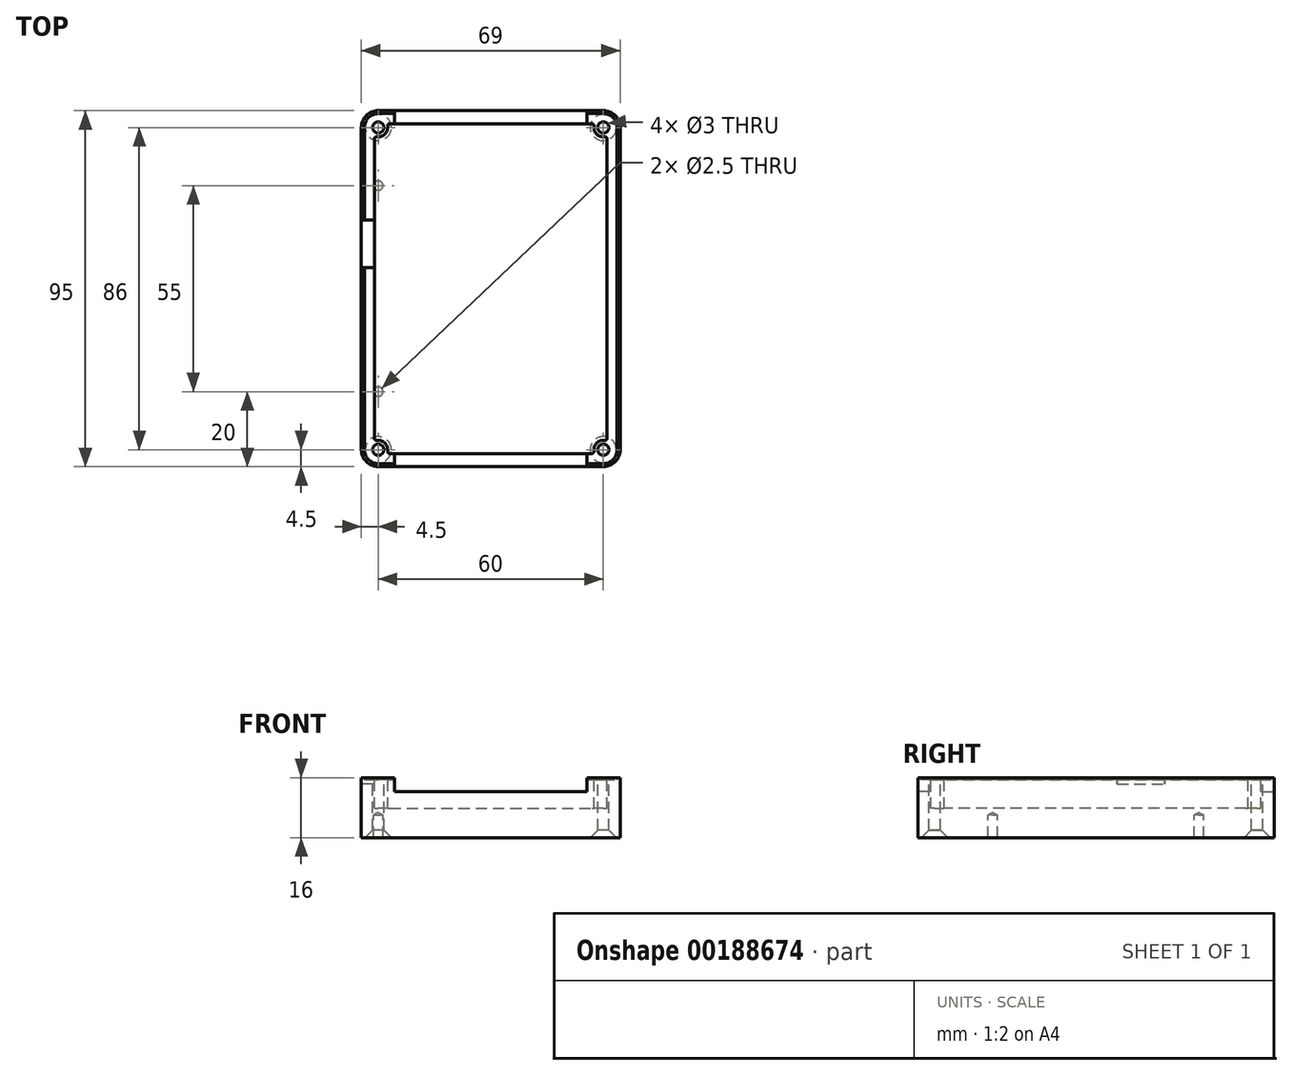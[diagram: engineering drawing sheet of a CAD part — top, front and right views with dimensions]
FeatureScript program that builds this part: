
annotation { "Feature Type Name" : "Feature", "Feature Type Description" : "" }
export const myFeature = defineFeature(function(context is Context, id is Id, definition is map)
    precondition{}
    {
        {
            var Q0;
            Q0=qCreatedBy(makeId("Top.planeOp"),FACE);
            var sketch = newSketch(context, id + "F0", { "sketchPlane" : qUnion([Q0])});
            skLineSegment(sketch, "E0.bottom", {"start": v(34.5, 47.5) * mm, "end": v(-34.5, 47.5) * mm});
            skLineSegment(sketch, "E0.top", {"start": v(34.5, -47.5) * mm, "end": v(-34.5, -47.5) * mm});
            skLineSegment(sketch, "E0.left", {"start": v(34.5, 47.5) * mm, "end": v(34.5, -47.5) * mm});
            skLineSegment(sketch, "E0.right", {"start": v(-34.5, 47.5) * mm, "end": v(-34.5, -47.5) * mm});
            skPoint(sketch, "E0.middle", {"position": v(0, 0) * mm});
            skSolve(sketch);
        }
        {
            var Q0;
            Q0=makeQuery(id+"F0.imprint","IMPRINT",FACE,{"disambiguationData":[TD([[makeQuery(id+"F0.imprint","IMPRINT",EDGE,{"derivedFrom":sQuery(id+"F0.wireOp",EDGE,"E0.bottom")}),1.0]])]});
            extrude(context, id + "F1", {"entities" : qUnion([Q0]), "flatOperationType" : FlatOperationType.REMOVE, "offsetDistance" : 25 * mm, "depth" : 15.5 * mm, "domain" : OperationDomain.MODEL});
        }
        {
            var Q0;
            Q0=makeQuery(id+"F1.opExtrude","SWEPT_EDGE",EDGE,{"disambiguationData":[OSD([sQuery(id+"F0.wireOp",EDGE,"E0.bottom"),sQuery(id+"F0.wireOp",EDGE,"E0.right")])]});
            var Q1;
            Q1=makeQuery(id+"F1.opExtrude","SWEPT_EDGE",EDGE,{"disambiguationData":[OSD([sQuery(id+"F0.wireOp",EDGE,"E0.top"),sQuery(id+"F0.wireOp",EDGE,"E0.right")])]});
            var Q2;
            Q2=makeQuery(id+"F1.opExtrude","SWEPT_EDGE",EDGE,{"disambiguationData":[OSD([sQuery(id+"F0.wireOp",EDGE,"E0.top"),sQuery(id+"F0.wireOp",EDGE,"E0.left")])]});
            var Q3;
            Q3=makeQuery(id+"F1.opExtrude","SWEPT_EDGE",EDGE,{"disambiguationData":[OSD([sQuery(id+"F0.wireOp",EDGE,"E0.bottom"),sQuery(id+"F0.wireOp",EDGE,"E0.left")])]});
            fillet(context, id + "F2", {"entities" : qUnion([Q0, Q1, Q2, Q3]), "radius" : 4.5 * mm, "tangentPropagation" : true, "allowEdgeOverflow" : false});
        }
        {
            var Q0;
            Q0=makeQuery(id+"F1.opExtrude","CAP_FACE",FACE,{"disambiguationData":[OSD([sQuery(id+"F0.wireOp",EDGE,"E0.bottom"),sQuery(id+"F0.wireOp",EDGE,"E0.top"),sQuery(id+"F0.wireOp",EDGE,"E0.left"),sQuery(id+"F0.wireOp",EDGE,"E0.right")])],"isStart":false});
            var sketch = newSketch(context, id + "F3", { "sketchPlane" : qUnion([Q0])});
            skArc(sketch, "E1", {"start": v(-30, 40.5) * mm, "mid": v(-28.23, 41.23) * mm, "end": v(-27.5, 43) * mm});
            skArc(sketch, "E2", {"start": v(27.5, 43) * mm, "mid": v(28.23, 41.23) * mm, "end": v(30, 40.5) * mm});
            skArc(sketch, "E3", {"start": v(30, -40.5) * mm, "mid": v(28.23, -41.23) * mm, "end": v(27.5, -43) * mm});
            skArc(sketch, "E4", {"start": v(-27.5, -43) * mm, "mid": v(-28.23, -41.23) * mm, "end": v(-30, -40.5) * mm});
            skLineSegment(sketch, "E5", {"start": v(-30, 40.5) * mm, "end": v(-31, 40.5) * mm});
            skLineSegment(sketch, "E6", {"start": v(-31, 40.5) * mm, "end": v(-31, -40.5) * mm});
            skLineSegment(sketch, "E7", {"start": v(-31, -40.5) * mm, "end": v(-30, -40.5) * mm});
            skLineSegment(sketch, "E8", {"start": v(-27.5, -43) * mm, "end": v(-27.5, -44) * mm});
            skLineSegment(sketch, "E9", {"start": v(-27.5, -44) * mm, "end": v(27.5, -44) * mm});
            skLineSegment(sketch, "E10", {"start": v(27.5, -44) * mm, "end": v(27.5, -43) * mm});
            skLineSegment(sketch, "E11", {"start": v(30, -40.5) * mm, "end": v(31, -40.5) * mm});
            skLineSegment(sketch, "E12", {"start": v(31, -40.5) * mm, "end": v(31, 40.5) * mm});
            skLineSegment(sketch, "E13", {"start": v(31, 40.5) * mm, "end": v(30, 40.5) * mm});
            skLineSegment(sketch, "E14", {"start": v(27.5, 43) * mm, "end": v(27.5, 44) * mm});
            skLineSegment(sketch, "E15", {"start": v(27.5, 44) * mm, "end": v(-27.5, 44) * mm});
            skLineSegment(sketch, "E16", {"start": v(-27.5, 44) * mm, "end": v(-27.5, 43) * mm});
            skPoint(sketch, "E17.0", {"position": v(33.18, 46.18) * mm});
            skLineSegment(sketch, "E18.bottom", {"start": v(31, 44) * mm, "end": v(-31, 44) * mm, "construction": true});
            skLineSegment(sketch, "E18.top", {"start": v(31, -44) * mm, "end": v(-31, -44) * mm, "construction": true});
            skLineSegment(sketch, "E18.left", {"start": v(31, 44) * mm, "end": v(31, -44) * mm, "construction": true});
            skLineSegment(sketch, "E18.right", {"start": v(-31, 44) * mm, "end": v(-31, -44) * mm, "construction": true});
            skPoint(sketch, "E18.middle", {"position": v(0, 0) * mm});
            skSolve(sketch);
        }
        {
            var Q0;
            Q0=makeQuery(id+"F3.imprint","IMPRINT",FACE,{"disambiguationData":[TD([[makeQuery(id+"F3.imprint","IMPRINT",EDGE,{"derivedFrom":sQuery(id+"F3.wireOp",EDGE,"E1")}),-1.0]])]});
            extrude(context, id + "F4", {"entities" : qUnion([Q0]), "operationType" : NewBodyOperationType.REMOVE, "flatOperationType" : FlatOperationType.REMOVE, "oppositeDirection" : true, "offsetDistance" : 25 * mm, "depth" : (15.5 - 7.8) * mm, "domain" : OperationDomain.MODEL});
        }
        {
            var Q0;
            Q0=makeQuery(id+"F3.imprint","IMPRINT",FACE,{"disambiguationData":[TD([[makeQuery(id+"F3.imprint","IMPRINT",EDGE,{"derivedFrom":sQuery(id+"F3.wireOp",EDGE,"E1")}),1.0]])]});
            var sketch = newSketch(context, id + "F5", { "sketchPlane" : qUnion([Q0])});
            skLineSegment(sketch, "E19.0", {"start": v(-34.5, 43) * mm, "end": v(-34.5, -43) * mm});
            skArc(sketch, "E19.1", {"start": v(-30, 47.5) * mm, "mid": v(-33.18, 46.18) * mm, "end": v(-34.5, 43) * mm});
            skLineSegment(sketch, "E19.2", {"start": v(30, 47.5) * mm, "end": v(-30, 47.5) * mm});
            skLineSegment(sketch, "E19.3", {"start": v(34.5, 43) * mm, "end": v(34.5, -43) * mm});
            skArc(sketch, "E19.4", {"start": v(34.5, 43) * mm, "mid": v(33.18, 46.18) * mm, "end": v(30, 47.5) * mm});
            skArc(sketch, "E19.5", {"start": v(30, -47.5) * mm, "mid": v(33.18, -46.18) * mm, "end": v(34.5, -43) * mm});
            skLineSegment(sketch, "E19.6", {"start": v(30, -47.5) * mm, "end": v(-30, -47.5) * mm});
            skArc(sketch, "E19.7", {"start": v(-34.5, -43) * mm, "mid": v(-33.18, -46.18) * mm, "end": v(-30, -47.5) * mm});
            skLineSegment(sketch, "E20.0", {"start": v(30, 46.7) * mm, "end": v(-30, 46.7) * mm});
            skArc(sketch, "E20.1", {"start": v(33.7, 43) * mm, "mid": v(32.62, 45.62) * mm, "end": v(30, 46.7) * mm});
            skArc(sketch, "E20.2", {"start": v(-30, 46.7) * mm, "mid": v(-32.62, 45.62) * mm, "end": v(-33.7, 43) * mm});
            skLineSegment(sketch, "E20.3", {"start": v(33.7, 43) * mm, "end": v(33.7, -43) * mm});
            skLineSegment(sketch, "E20.4", {"start": v(-33.7, 43) * mm, "end": v(-33.7, -43) * mm});
            skArc(sketch, "E20.5", {"start": v(-33.7, -43) * mm, "mid": v(-32.62, -45.62) * mm, "end": v(-30, -46.7) * mm});
            skLineSegment(sketch, "E20.6", {"start": v(30, -46.7) * mm, "end": v(-30, -46.7) * mm});
            skArc(sketch, "E20.7", {"start": v(30, -46.7) * mm, "mid": v(32.62, -45.62) * mm, "end": v(33.7, -43) * mm});
            skSolve(sketch);
        }
        {
            var Q0;
            Q0 = qSketchRegion(id + "F5", true);
            extrude(context, id + "F6", {"entities" : qUnion([Q0]), "operationType" : NewBodyOperationType.ADD, "depth" : 0.5 * mm});
        }
        {
            var Q0;
            Q0=makeQuery(id+"FRwk8FVEWLEbkhO_1.boolean.opBoolean","MERGE",EDGE,{"derivedFrom":[makeQuery(id+"F4.boolean.opBoolean","COPY",EDGE,{"derivedFrom":makeQuery(id+"F4.opExtrude","SWEPT_EDGE",EDGE,{"disambiguationData":[OSD([sQuery(id+"F3.wireOp",EDGE,"E5"),sQuery(id+"F3.wireOp",EDGE,"E6")])]})}),makeQuery(id+"FRwk8FVEWLEbkhO_1.opExtrude","SWEPT_EDGE",EDGE,{"disambiguationData":[OSD([sQuery(id+"FsmA3quXVaOsy4H_1.wireOp",EDGE,"f00bc3e8-88e0-4702-8d79-10860423b05f.1"),sQuery(id+"FsmA3quXVaOsy4H_1.wireOp",EDGE,"f00bc3e8-88e0-4702-8d79-10860423b05f.2")])]})]});
            var Q1;
            Q1=makeQuery(id+"FRwk8FVEWLEbkhO_1.boolean.opBoolean","MERGE",EDGE,{"derivedFrom":[makeQuery(id+"F4.boolean.opBoolean","COPY",EDGE,{"derivedFrom":makeQuery(id+"F4.opExtrude","SWEPT_EDGE",EDGE,{"disambiguationData":[OSD([sQuery(id+"F3.wireOp",EDGE,"E15"),sQuery(id+"F3.wireOp",EDGE,"E16")])]})}),makeQuery(id+"FRwk8FVEWLEbkhO_1.opExtrude","SWEPT_EDGE",EDGE,{"disambiguationData":[OSD([sQuery(id+"FsmA3quXVaOsy4H_1.wireOp",EDGE,"f00bc3e8-88e0-4702-8d79-10860423b05f.3"),sQuery(id+"FsmA3quXVaOsy4H_1.wireOp",EDGE,"FdM2ibMO-9ZGO-dDVi-LVml-EPcpEFeJbmP4")])]})]});
            var Q2;
            Q2=makeQuery(id+"F4.boolean.opBoolean","COPY",EDGE,{"derivedFrom":makeQuery(id+"F4.opExtrude","SWEPT_EDGE",EDGE,{"disambiguationData":[OSD([sQuery(id+"F3.wireOp",EDGE,"E14"),sQuery(id+"F3.wireOp",EDGE,"E15")])]})});
            var Q3;
            Q3=makeQuery(id+"F4.boolean.opBoolean","COPY",EDGE,{"derivedFrom":makeQuery(id+"F4.opExtrude","SWEPT_EDGE",EDGE,{"disambiguationData":[OSD([sQuery(id+"F3.wireOp",EDGE,"E12"),sQuery(id+"F3.wireOp",EDGE,"E13")])]})});
            var Q4;
            Q4=makeQuery(id+"F4.boolean.opBoolean","COPY",EDGE,{"derivedFrom":makeQuery(id+"F4.opExtrude","SWEPT_EDGE",EDGE,{"disambiguationData":[OSD([sQuery(id+"F3.wireOp",EDGE,"E11"),sQuery(id+"F3.wireOp",EDGE,"E12")])]})});
            var Q5;
            Q5=makeQuery(id+"F4.boolean.opBoolean","COPY",EDGE,{"derivedFrom":makeQuery(id+"F4.opExtrude","SWEPT_EDGE",EDGE,{"disambiguationData":[OSD([sQuery(id+"F3.wireOp",EDGE,"E9"),sQuery(id+"F3.wireOp",EDGE,"E10")])]})});
            var Q6;
            Q6=makeQuery(id+"FRwk8FVEWLEbkhO_1.boolean.opBoolean","MERGE",EDGE,{"derivedFrom":[makeQuery(id+"F4.boolean.opBoolean","COPY",EDGE,{"derivedFrom":makeQuery(id+"F4.opExtrude","SWEPT_EDGE",EDGE,{"disambiguationData":[OSD([sQuery(id+"F3.wireOp",EDGE,"E8"),sQuery(id+"F3.wireOp",EDGE,"E9")])]})}),makeQuery(id+"FRwk8FVEWLEbkhO_1.opExtrude","SWEPT_EDGE",EDGE,{"disambiguationData":[OSD([sQuery(id+"FsmA3quXVaOsy4H_1.wireOp",EDGE,"f00bc3e8-88e0-4702-8d79-10860423b05f.6"),sQuery(id+"FsmA3quXVaOsy4H_1.wireOp",EDGE,"e3dDnFLk-rLFV-1gcz-UCYJ-rSUwsOXShIx1")])]})]});
            var Q7;
            Q7=makeQuery(id+"FRwk8FVEWLEbkhO_1.boolean.opBoolean","MERGE",EDGE,{"derivedFrom":[makeQuery(id+"F4.boolean.opBoolean","COPY",EDGE,{"derivedFrom":makeQuery(id+"F4.opExtrude","SWEPT_EDGE",EDGE,{"disambiguationData":[OSD([sQuery(id+"F3.wireOp",EDGE,"E6"),sQuery(id+"F3.wireOp",EDGE,"E7")])]})}),makeQuery(id+"FRwk8FVEWLEbkhO_1.opExtrude","SWEPT_EDGE",EDGE,{"disambiguationData":[OSD([sQuery(id+"FsmA3quXVaOsy4H_1.wireOp",EDGE,"f00bc3e8-88e0-4702-8d79-10860423b05f.1"),sQuery(id+"FsmA3quXVaOsy4H_1.wireOp",EDGE,"f00bc3e8-88e0-4702-8d79-10860423b05f.4")])]})]});
            fillet(context, id + "F7", {"entities" : qUnion([Q0, Q1, Q2, Q3, Q4, Q5, Q6, Q7]), "radius" : 0.5 * mm, "tangentPropagation" : true, "allowEdgeOverflow" : false});
        }
        {
            var Q0;
            Q0=makeQuery(id+"F1.opExtrude","CAP_FACE",FACE,{"disambiguationData":[OSD([sQuery(id+"F0.wireOp",EDGE,"E0.bottom"),sQuery(id+"F0.wireOp",EDGE,"E0.top"),sQuery(id+"F0.wireOp",EDGE,"E0.left"),sQuery(id+"F0.wireOp",EDGE,"E0.right")])],"isStart":true});
            var sketch = newSketch(context, id + "F8", { "sketchPlane" : qUnion([Q0])});
            skPoint(sketch, "E21", {"position": v(-30, 27.5) * mm});
            skPoint(sketch, "E22", {"position": v(-30, -27.5) * mm});
            skPoint(sketch, "E23", {"position": v(-30, 43) * mm});
            skPoint(sketch, "E24", {"position": v(30, 43) * mm});
            skPoint(sketch, "E25", {"position": v(30, -43) * mm});
            skPoint(sketch, "E26", {"position": v(-30, -43) * mm});
            skSolve(sketch);
        }
        {
            var Q0;
            Q0=makeQuery(id+"F6.boolean.opBoolean","MERGE",FACE,{"derivedFrom":[makeQuery(id+"F1.opExtrude","SWEPT_FACE",FACE,{"disambiguationData":[OSD([sQuery(id+"F0.wireOp",EDGE,"E0.bottom")])]}),makeQuery(id+"F6.opExtrude","SWEPT_FACE",FACE,{"disambiguationData":[OSD([sQuery(id+"F5.wireOp",EDGE,"E19.2")])]})]});
            var sketch = newSketch(context, id + "F9", { "sketchPlane" : qUnion([Q0])});
            skLineSegment(sketch, "E27.bottom", {"start": v(-25.6, 16) * mm, "end": v(25.6, 16) * mm});
            skLineSegment(sketch, "E27.top", {"start": v(-25.6, 12.3) * mm, "end": v(25.6, 12.3) * mm});
            skLineSegment(sketch, "E27.left", {"start": v(-25.6, 16) * mm, "end": v(-25.6, 12.3) * mm});
            skLineSegment(sketch, "E27.right", {"start": v(25.6, 16) * mm, "end": v(25.6, 12.3) * mm});
            skSolve(sketch);
        }
        {
            var Q0;
            Q0 = qSketchRegion(id + "F9", true);
            var Q1;
            Q1=makeQuery(id+"FRwk8FVEWLEbkhO_1.boolean.opBoolean","MERGE",FACE,{"derivedFrom":[makeQuery(id+"F4.boolean.opBoolean","COPY",FACE,{"derivedFrom":makeQuery(id+"F4.opExtrude","SWEPT_FACE",FACE,{"disambiguationData":[OSD([sQuery(id+"F3.wireOp",EDGE,"E15")])]})}),makeQuery(id+"FRwk8FVEWLEbkhO_1.opExtrude","SWEPT_FACE",FACE,{"disambiguationData":[OSD([sQuery(id+"FsmA3quXVaOsy4H_1.wireOp",EDGE,"FdM2ibMO-9ZGO-dDVi-LVml-EPcpEFeJbmP4")])]})]});
            extrude(context, id + "F10", {"entities" : qUnion([Q0]), "operationType" : NewBodyOperationType.REMOVE, "endBound" : BoundingType.UP_TO_SURFACE, "oppositeDirection" : true, "endBoundEntityFace" : qUnion([Q1]), "depth" : 25 * mm});
        }
        {
            var Q0;
            Q0=makeQuery(id+"F6.boolean.opBoolean","MERGE",FACE,{"derivedFrom":[makeQuery(id+"F1.opExtrude","SWEPT_FACE",FACE,{"disambiguationData":[OSD([sQuery(id+"F0.wireOp",EDGE,"E0.top")])]}),makeQuery(id+"F6.opExtrude","SWEPT_FACE",FACE,{"disambiguationData":[OSD([sQuery(id+"F5.wireOp",EDGE,"E19.6")])]})]});
            var sketch = newSketch(context, id + "F11", { "sketchPlane" : qUnion([Q0])});
            skLineSegment(sketch, "E28.0", {"start": v(25.6, 12.3) * mm, "end": v(-25.6, 12.3) * mm});
            skLineSegment(sketch, "E29.0", {"start": v(-25.6, 16) * mm, "end": v(-25.6, 12.3) * mm});
            skLineSegment(sketch, "E30.0", {"start": v(25.6, 16) * mm, "end": v(25.6, 12.3) * mm});
            skLineSegment(sketch, "E31.0", {"start": v(25.6, 16) * mm, "end": v(-25.6, 16) * mm});
            skSolve(sketch);
        }
        {
            var Q0;
            Q0 = qSketchRegion(id + "F11", true);
            var Q1;
            Q1=makeQuery(id+"FRwk8FVEWLEbkhO_1.boolean.opBoolean","MERGE",FACE,{"derivedFrom":[makeQuery(id+"F4.boolean.opBoolean","COPY",FACE,{"derivedFrom":makeQuery(id+"F4.opExtrude","SWEPT_FACE",FACE,{"disambiguationData":[OSD([sQuery(id+"F3.wireOp",EDGE,"E9")])]})}),makeQuery(id+"FRwk8FVEWLEbkhO_1.opExtrude","SWEPT_FACE",FACE,{"disambiguationData":[OSD([sQuery(id+"FsmA3quXVaOsy4H_1.wireOp",EDGE,"e3dDnFLk-rLFV-1gcz-UCYJ-rSUwsOXShIx1")])]})]});
            extrude(context, id + "F12", {"entities" : qUnion([Q0]), "operationType" : NewBodyOperationType.REMOVE, "flatOperationType" : FlatOperationType.REMOVE, "endBound" : BoundingType.UP_TO_SURFACE, "oppositeDirection" : true, "endBoundEntityFace" : qUnion([Q1]), "offsetDistance" : 25 * mm, "depth" : 25 * mm, "domain" : OperationDomain.MODEL});
        }
        {
            var Q0;
            Q0=sQuery(id+"F8.wireOp",VERTEX,"E21");
            var Q1;
            Q1=sQuery(id+"F8.wireOp",VERTEX,"E22");
            var Q2;
            Q2=makeQuery(id+"F1.opExtrude","SWEPT_BODY",BODY,{"disambiguationData":[OSD([sQuery(id+"F0.wireOp",EDGE,"E0.bottom"),sQuery(id+"F0.wireOp",EDGE,"E0.top"),sQuery(id+"F0.wireOp",EDGE,"E0.left"),sQuery(id+"F0.wireOp",EDGE,"E0.right")])]});
            hole(context, id + "F13", {"style" : HoleStyle.SIMPLE, "endStyle" : HoleEndStyle.BLIND, "holeDiameter" : 2.5 * mm, "holeDepth" : 6 * mm, "tappedDepth" : 12 * mm, "tapClearance" : 3, "locations" : qUnion([Q0, Q1]), "scope" : qUnion([Q2]), "majorDiameter" : 5 * mm, "startStyle" : HoleStartStyle.SKETCH});
        }
        {
            var Q0;
            Q0=sQuery(id+"F8.wireOp",VERTEX,"E24");
            var Q1;
            Q1=sQuery(id+"F8.wireOp",VERTEX,"E25");
            var Q2;
            Q2=sQuery(id+"F8.wireOp",VERTEX,"E23");
            var Q3;
            Q3=sQuery(id+"F8.wireOp",VERTEX,"E26");
            var Q4;
            Q4=makeQuery(id+"F1.opExtrude","SWEPT_BODY",BODY,{"disambiguationData":[OSD([sQuery(id+"F0.wireOp",EDGE,"E0.bottom"),sQuery(id+"F0.wireOp",EDGE,"E0.top"),sQuery(id+"F0.wireOp",EDGE,"E0.left"),sQuery(id+"F0.wireOp",EDGE,"E0.right")])]});
            hole(context, id + "F14", {"style" : HoleStyle.C_SINK, "endStyle" : HoleEndStyle.THROUGH, "holeDiameter" : 3 * mm, "cSinkDiameter" : 7 * mm, "cSinkAngle" : 90 * degree, "tappedDepth" : 12 * mm, "tapClearance" : 3, "locations" : qUnion([Q0, Q1, Q2, Q3]), "scope" : qUnion([Q4]), "startStyle" : HoleStartStyle.PART});
        }
        {
            var Q0;
            Q0=makeQuery(id+"F6.boolean.opBoolean","MERGE",FACE,{"derivedFrom":[makeQuery(id+"F1.opExtrude","SWEPT_FACE",FACE,{"disambiguationData":[OSD([sQuery(id+"F0.wireOp",EDGE,"E0.right")])]}),makeQuery(id+"F6.opExtrude","SWEPT_FACE",FACE,{"disambiguationData":[OSD([sQuery(id+"F5.wireOp",EDGE,"E19.0")])]})]});
            var sketch = newSketch(context, id + "F15", { "sketchPlane" : qUnion([Q0])});
            skLineSegment(sketch, "E32.bottom", {"start": v(-18.35, 16) * mm, "end": v(-5.65, 16) * mm});
            skLineSegment(sketch, "E32.top", {"start": v(-18.35, 14.32) * mm, "end": v(-5.65, 14.32) * mm});
            skLineSegment(sketch, "E32.left", {"start": v(-18.35, 16) * mm, "end": v(-18.35, 14.32) * mm});
            skLineSegment(sketch, "E32.right", {"start": v(-5.65, 16) * mm, "end": v(-5.65, 14.32) * mm});
            skSolve(sketch);
        }
        {
            var Q0;
            Q0=makeQuery(id+"F15.imprint","IMPRINT",FACE,{"disambiguationData":[TD([[makeQuery(id+"F15.imprint","IMPRINT",EDGE,{"derivedFrom":sQuery(id+"F15.wireOp",EDGE,"E32.bottom")}),-1.0]])]});
            extrude(context, id + "F16", {"entities" : qUnion([Q0]), "operationType" : NewBodyOperationType.REMOVE, "endBound" : BoundingType.UP_TO_NEXT, "oppositeDirection" : true, "depth" : 25 * mm, "offsetDistance" : 25 * mm});
        }
    });
